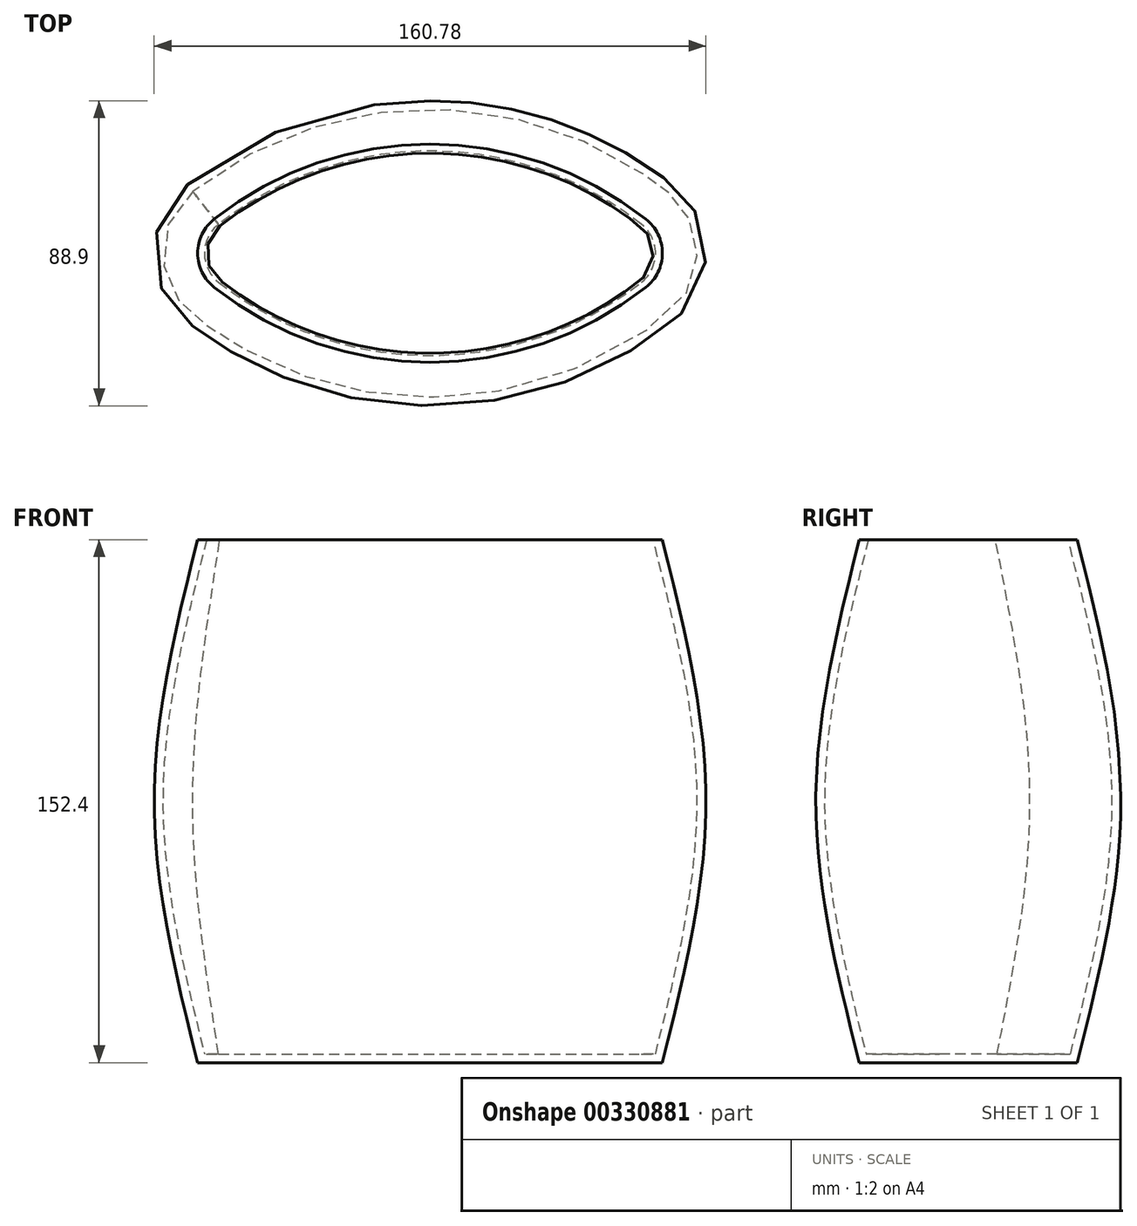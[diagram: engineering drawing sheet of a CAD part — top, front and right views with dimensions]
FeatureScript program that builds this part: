
annotation { "Feature Type Name" : "Feature", "Feature Type Description" : "" }
export const myFeature = defineFeature(function(context is Context, id is Id, definition is map)
    precondition{}
    {
        {
            var Q0;
            Q0=qCreatedBy(makeId("Top.planeOp"),FACE);
            var sketch = newSketch(context, id + "F0", { "sketchPlane" : qUnion([Q0])});
            skArc(sketch, "E0", {"start": v(-62.85, 9.98) * mm, "mid": v(-67.7, 0) * mm, "end": v(-62.85, -9.98) * mm});
            skArc(sketch, "E1", {"start": v(62.85, -9.98) * mm, "mid": v(67.7, 0) * mm, "end": v(62.85, 9.98) * mm});
            skArc(sketch, "E2", {"start": v(62.85, 9.98) * mm, "mid": v(0, 31.75) * mm, "end": v(-62.85, 9.98) * mm});
            skArc(sketch, "E3", {"start": v(-62.85, -9.98) * mm, "mid": v(0, -31.75) * mm, "end": v(62.85, -9.98) * mm});
            skSolve(sketch);
        }
        {
            var Q0;
            Q0=qCreatedBy(makeId("Top.planeOp"),FACE);
            cPlane(context, id + "F1", {"entities" : qUnion([Q0]), "cplaneType" : CPlaneType.OFFSET, "offset" : 76.2 * mm, "width" : 152.4 * mm, "height" : 152.4 * mm});
        }
        {
            var Q0;
            Q0=qCreatedBy(id+"F1.planeOp",FACE);
            var sketch = newSketch(context, id + "F2", { "sketchPlane" : qUnion([Q0])});
            skArc(sketch, "E4.0", {"start": v(70.7, 19.96) * mm, "mid": v(0, 44.45) * mm, "end": v(-70.7, 19.96) * mm});
            skArc(sketch, "E4.1", {"start": v(70.7, -19.96) * mm, "mid": v(80.4, 0) * mm, "end": v(70.7, 19.96) * mm});
            skArc(sketch, "E4.2", {"start": v(-70.7, -19.96) * mm, "mid": v(0, -44.45) * mm, "end": v(70.7, -19.96) * mm});
            skArc(sketch, "E4.3", {"start": v(-70.7, 19.96) * mm, "mid": v(-80.4, 0) * mm, "end": v(-70.7, -19.96) * mm});
            skSolve(sketch);
        }
        {
            var Q0;
            Q0=qCreatedBy(id+"F1.planeOp",FACE);
            cPlane(context, id + "F3", {"entities" : qUnion([Q0]), "cplaneType" : CPlaneType.OFFSET, "offset" : 76.2 * mm, "width" : 152.4 * mm, "height" : 152.4 * mm});
        }
        {
            var Q0;
            Q0=qCreatedBy(id+"F3.planeOp",FACE);
            var sketch = newSketch(context, id + "F4", { "sketchPlane" : qUnion([Q0])});
            skArc(sketch, "E5.0", {"start": v(-62.85, -9.98) * mm, "mid": v(0, -31.75) * mm, "end": v(62.85, -9.98) * mm});
            skArc(sketch, "E6.0", {"start": v(62.85, -9.98) * mm, "mid": v(67.7, 0) * mm, "end": v(62.85, 9.98) * mm});
            skArc(sketch, "E7.0", {"start": v(62.85, 9.98) * mm, "mid": v(0, 31.75) * mm, "end": v(-62.85, 9.98) * mm});
            skArc(sketch, "E8.0", {"start": v(-62.85, 9.98) * mm, "mid": v(-67.7, 0) * mm, "end": v(-62.85, -9.98) * mm});
            skSolve(sketch);
        }
        {
            var Q0;
            Q0=makeQuery(id+"F0.imprint","IMPRINT",FACE,{"disambiguationData":[TD([[makeQuery(id+"F0.imprint","IMPRINT",EDGE,{"derivedFrom":sQuery(id+"F0.wireOp",EDGE,"E0")}),1.0]])]});
            var Q1;
            Q1=makeQuery(id+"F2.imprint","IMPRINT",FACE,{"disambiguationData":[TD([[makeQuery(id+"F2.imprint","IMPRINT",EDGE,{"derivedFrom":sQuery(id+"F2.wireOp",EDGE,"E4.0")}),1.0]])]});
            var Q2;
            Q2=makeQuery(id+"F4.imprint","IMPRINT",FACE,{"disambiguationData":[TD([[makeQuery(id+"F4.imprint","IMPRINT",EDGE,{"derivedFrom":sQuery(id+"F4.wireOp",EDGE,"E5.0")}),1.0]])]});
            loft(context, id + "F5", {"sheetProfilesArray" : [{ "sheetProfileEntities" : qUnion([Q0]) }, { "sheetProfileEntities" : qUnion([Q1]) }, { "sheetProfileEntities" : qUnion([Q2]) }]});
        }
        {
            var Q0;
            Q0=makeQuery(id+"F5.opLoft","CAP_FACE",FACE,{"disambiguationData":[OSD([makeQuery(id+"F4.imprint","IMPRINT",FACE,{"disambiguationData":[TD([[makeQuery(id+"F4.imprint","IMPRINT",EDGE,{"derivedFrom":sQuery(id+"F4.wireOp",EDGE,"E5.0")}),1.0]])]})])],"isStart":true});
            shell(context, id + "F6", {"entities" : qUnion([Q0]), "thickness" : 2.54 * mm});
        }
    });
